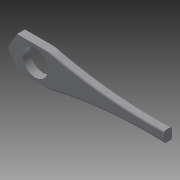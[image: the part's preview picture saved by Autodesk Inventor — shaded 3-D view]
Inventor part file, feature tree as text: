
AUTODESK INVENTOR PART (.ipt)
format: ipt  version: 2015 (Build 190159000, 159)  size: 130,560 bytes
history: native  units: mm
features: fillet x4, extrude x3, sketch x3
ambient origin geometry x8: Origin, YZ Plane, XZ Plane, XY Plane, X Axis, Y Axis, Z Axis, Center Point
bodies: Solid1 (feature_tree)
feature tree (10):
  extrude  "Extrusion1"  Depth=3.0mm
  extrude  "Extrusion2"  Depth=10.0mm
  fillet  "Fillet1"  Radius=130.0mm
  fillet  "Fillet2"  Radius=7.0mm
  fillet  "Fillet3"  Radius=5.0mm
  fillet  "Fillet4"  Radius=10.0mm
  extrude  "Extrusion3"  Depth=380.0mm
  sketch  "Sketch1"  dims[d0=22.25mm d1=3.0mm]
  sketch  "Sketch2"  dims[d2=3.0mm d3=5.0mm d6=130.0mm d7=7.0mm d8=0.0mm d9=5.0mm d10=10.0mm]
  sketch  "Sketch3"  dims[d11=5.0mm d12=380.0mm d13=380.0mm d14=10.0mm d15=0.0mm d16=2.0mm d17=2.0mm d18=2.0mm d19=2.0mm d20=8.0mm d21=7.0mm d22=0.0mm]
